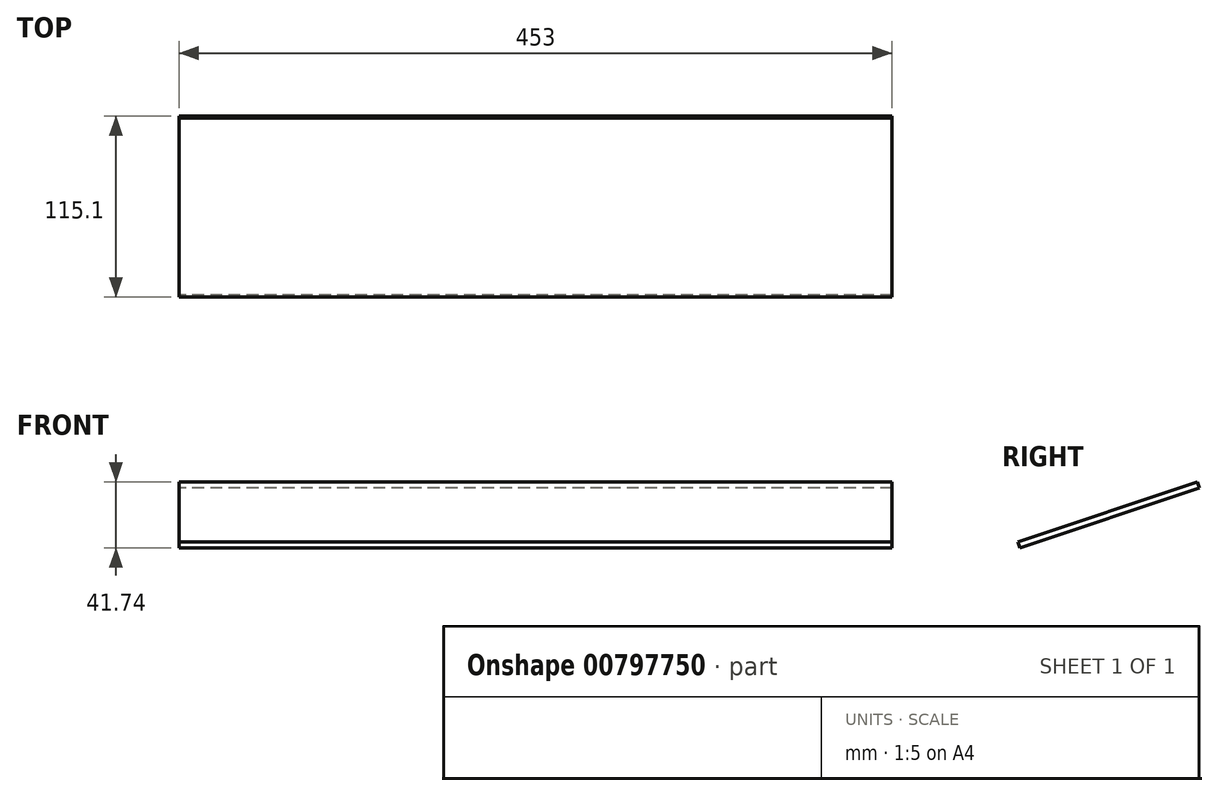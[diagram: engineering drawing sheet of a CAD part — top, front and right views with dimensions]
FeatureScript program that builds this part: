
annotation { "Feature Type Name" : "Feature", "Feature Type Description" : "" }
export const myFeature = defineFeature(function(context is Context, id is Id, definition is map)
    precondition{}
    {
        {
            var Q0;
            Q0=qCreatedBy(makeId("Right.planeOp"),FACE);
            var sketch = newSketch(context, id + "F0", { "sketchPlane" : qUnion([Q0])});
            skLineSegment(sketch, "E0", {"start": v(0, 0) * mm, "end": v(0, 80) * mm, "construction": true});
            skLineSegment(sketch, "E1", {"start": v(0, 80) * mm, "end": v(-54, 80) * mm, "construction": true});
            skLineSegment(sketch, "E2", {"start": v(-54, 80) * mm, "end": v(-54, 70) * mm, "construction": true});
            skLineSegment(sketch, "E3", {"start": v(-54, 70) * mm, "end": v(-168, 32) * mm, "construction": true});
            skLineSegment(sketch, "E4", {"start": v(-168, 32) * mm, "end": v(-168, 0) * mm, "construction": true});
            skLineSegment(sketch, "E5", {"start": v(-168, 0) * mm, "end": v(0, 0) * mm, "construction": true});
            skLineSegment(sketch, "E6", {"start": v(-54.16, 69.95) * mm, "end": v(-55.42, 73.74) * mm});
            skLineSegment(sketch, "E7", {"start": v(-55.42, 73.74) * mm, "end": v(-169.26, 35.8) * mm});
            skLineSegment(sketch, "E8", {"start": v(-169.26, 35.8) * mm, "end": v(-168, 32) * mm});
            skLineSegment(sketch, "E9", {"start": v(-168, 32) * mm, "end": v(-54.16, 69.95) * mm});
            skSolve(sketch);
        }
        {
            var Q0;
            Q0 = qSketchRegion(id + "F0", true);
            extrude(context, id + "F1", {"entities" : qUnion([Q0]), "depth" : 453 * mm, "offsetDistance" : 25 * mm});
        }
    });
